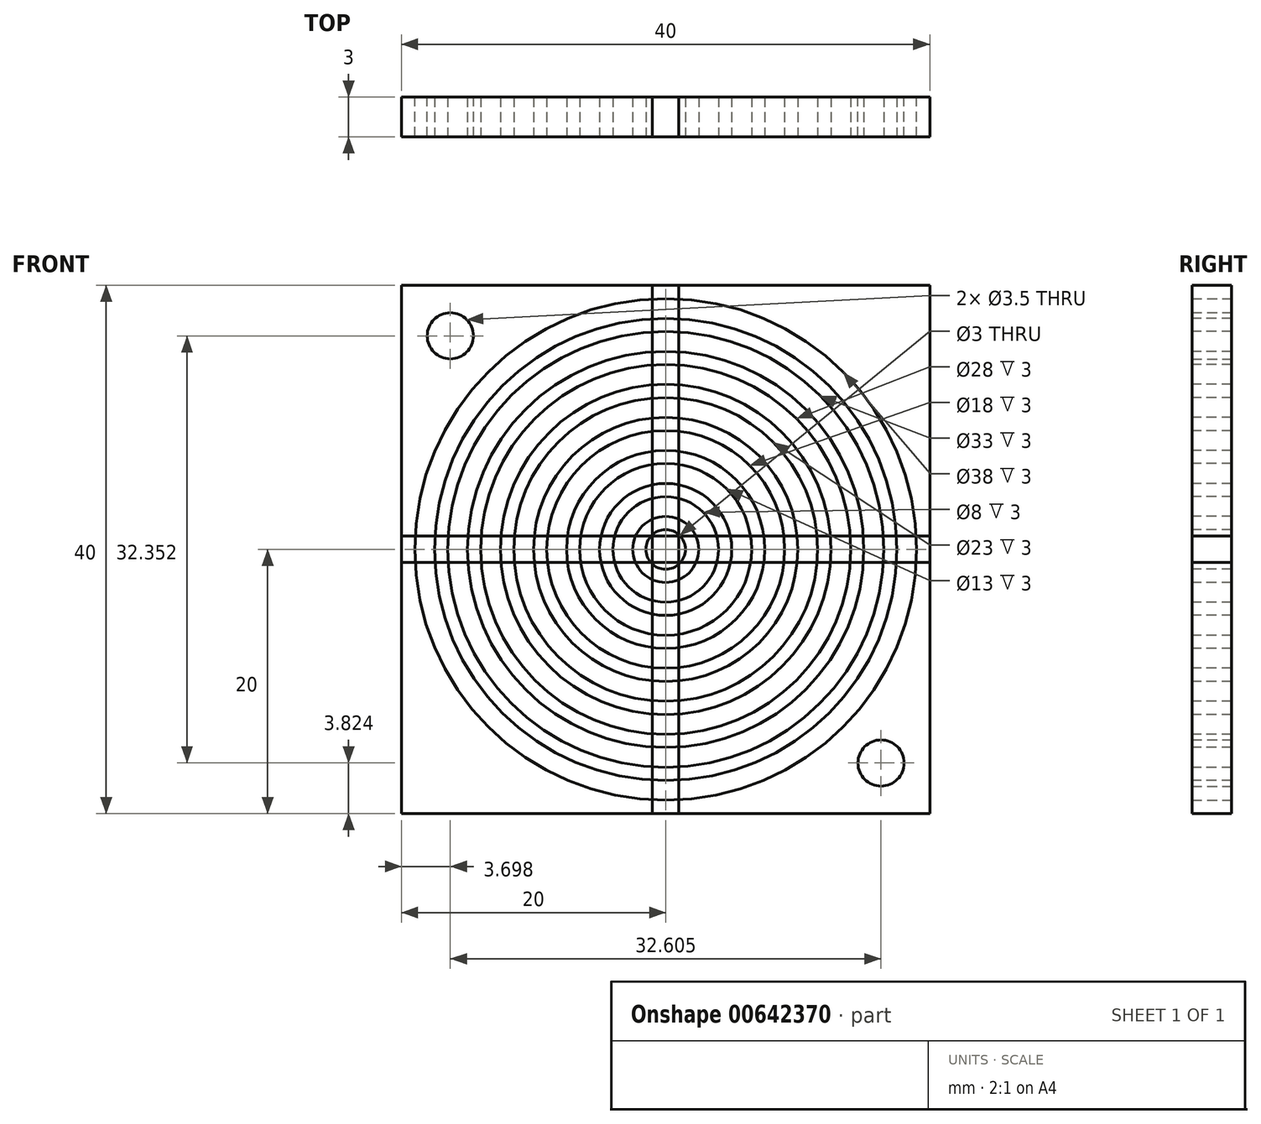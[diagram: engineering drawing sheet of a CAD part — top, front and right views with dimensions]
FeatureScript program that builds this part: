
annotation { "Feature Type Name" : "Feature", "Feature Type Description" : "" }
export const myFeature = defineFeature(function(context is Context, id is Id, definition is map)
    precondition{}
    {
        {
            var Q0;
            Q0=qCreatedBy(makeId("Front.planeOp"),FACE);
            var sketch = newSketch(context, id + "F0", { "sketchPlane" : qUnion([Q0])});
            skLineSegment(sketch, "E0.bottom", {"start": v(-20, 20) * mm, "end": v(20, 20) * mm});
            skLineSegment(sketch, "E0.top", {"start": v(-20, -20) * mm, "end": v(20, -20) * mm});
            skLineSegment(sketch, "E0.left", {"start": v(-20, 20) * mm, "end": v(-20, -20) * mm});
            skLineSegment(sketch, "E0.right", {"start": v(20, 20) * mm, "end": v(20, -20) * mm});
            skPoint(sketch, "E0.middle", {"position": v(0, 0) * mm});
            skCircle(sketch, "E1", {"center": v(0, 0) * mm, "radius": 19 * mm});
            skSolve(sketch);
        }
        {
            var Q0;
            Q0=qSketchRegion(id+"F0",true);
            extrude(context, id + "F1", {"entities" : qUnion([Q0]), "depth" : 3 * mm, "offsetDistance" : 25 * mm});
        }
        {
            var Q0;
            Q0=makeQuery(id+"F1.opExtrude","CAP_FACE",FACE,{"disambiguationData":[OSD([sQuery(id+"F0.wireOp",EDGE,"E0.bottom"),sQuery(id+"F0.wireOp",EDGE,"E0.top"),sQuery(id+"F0.wireOp",EDGE,"E0.left"),sQuery(id+"F0.wireOp",EDGE,"E0.right"),sQuery(id+"F0.wireOp",EDGE,"E1")])],"isStart":true});
            var sketch = newSketch(context, id + "F2", { "sketchPlane" : qUnion([Q0])});
            skCircle(sketch, "E2", {"center": v(16.3, 16.18) * mm, "radius": 1.75 * mm});
            skSolve(sketch);
        }
        {
            var Q0;
            Q0=qSketchRegion(id+"F2",true);
            extrude(context, id + "F3", {"entities" : qUnion([Q0]), "oppositeDirection" : true, "depth" : 5 * mm, "offsetDistance" : 25 * mm});
        }
        {
            var Q0;
            Q0=qCreatedBy(makeId("Top.planeOp"),FACE);
            var sketch = newSketch(context, id + "F5", { "sketchPlane" : qUnion([Q0])});
            skLineSegment(sketch, "E3", {"start": v(0, 9.6) * mm, "end": v(0, -20.04) * mm});
            skSolve(sketch);
        }
        {
            var Q0;
            Q0=makeQuery(id+"F3.opExtrude","SWEPT_BODY",BODY,{"disambiguationData":[OSD([sQuery(id+"F2.wireOp",EDGE,"E2")])]});
            var Q1;
            Q1=makeQuery(id+"F4.opExtrude","SWEPT_BODY",BODY,{"disambiguationData":[OSD([sQuery(id+"Fjy1AtXm3Dg5ggz_1.wireOp",EDGE,"P8TdTz7l-E2nd-Qza4-yqJy-pmsG0hgc4oyG")])]});
            var Q2;
            Q2=sQuery(id+"F5.wireOp",EDGE,"E3");
            circularPattern(context, id + "F6", {"entities" : qUnion([Q0, Q1]), "axis" : qUnion([Q2]), "angle" : 360 * degree, "instanceCount" : 2, "equalSpace" : true});
        }
        {
            var Q0;
            Q0=makeQuery(id+"F6.opPattern","COPY",BODY,{"derivedFrom":makeQuery(id+"F4.opExtrude","SWEPT_BODY",BODY,{"disambiguationData":[OSD([sQuery(id+"Fjy1AtXm3Dg5ggz_1.wireOp",EDGE,"P8TdTz7l-E2nd-Qza4-yqJy-pmsG0hgc4oyG")])]}),"instanceName":"1"});
            var Q1;
            Q1=makeQuery(id+"F6.opPattern","COPY",BODY,{"derivedFrom":makeQuery(id+"F3.opExtrude","SWEPT_BODY",BODY,{"disambiguationData":[OSD([sQuery(id+"F2.wireOp",EDGE,"E2")])]}),"instanceName":"1"});
            var Q2;
            Q2=makeQuery(id+"F4.opExtrude","SWEPT_BODY",BODY,{"disambiguationData":[OSD([sQuery(id+"Fjy1AtXm3Dg5ggz_1.wireOp",EDGE,"P8TdTz7l-E2nd-Qza4-yqJy-pmsG0hgc4oyG")])]});
            var Q3;
            Q3=makeQuery(id+"F3.opExtrude","SWEPT_BODY",BODY,{"disambiguationData":[OSD([sQuery(id+"F2.wireOp",EDGE,"E2")])]});
            var Q4;
            Q4=makeQuery(id+"F1.opExtrude","SWEPT_BODY",BODY,{"disambiguationData":[OSD([sQuery(id+"F0.wireOp",EDGE,"E0.bottom"),sQuery(id+"F0.wireOp",EDGE,"E0.top"),sQuery(id+"F0.wireOp",EDGE,"E0.left"),sQuery(id+"F0.wireOp",EDGE,"E0.right"),sQuery(id+"F0.wireOp",EDGE,"E1")])]});
            booleanBodies(context, id + "F7", {"operationType" : BooleanOperationType.SUBTRACTION, "tools" : qUnion([Q0, Q1, Q2, Q3]), "targets" : qUnion([Q4])});
        }
        {
            var Q0;
            Q0=makeQuery(id+"F1.opExtrude","CAP_FACE",FACE,{"disambiguationData":[OSD([sQuery(id+"F0.wireOp",EDGE,"E0.bottom"),sQuery(id+"F0.wireOp",EDGE,"E0.top"),sQuery(id+"F0.wireOp",EDGE,"E0.left"),sQuery(id+"F0.wireOp",EDGE,"E0.right"),sQuery(id+"F0.wireOp",EDGE,"E1")])],"isStart":false});
            var sketch = newSketch(context, id + "F8", { "sketchPlane" : qUnion([Q0])});
            skCircle(sketch, "E4", {"center": v(0, 0) * mm, "radius": 9 * mm});
            skCircle(sketch, "E5", {"center": v(0, 0) * mm, "radius": 10 * mm});
            skSolve(sketch);
        }
        {
            var Q0;
            Q0=makeQuery(id+"F8.imprint","IMPRINT",FACE,{"disambiguationData":[TD([[makeQuery(id+"F8.imprint","IMPRINT",EDGE,{"derivedFrom":makeQuery(id+"F1.opExtrude","CAP_EDGE",EDGE,{"disambiguationData":[OSD([sQuery(id+"F0.wireOp",EDGE,"E0.bottom")])],"isStart":false})}),-1.0]])]});
            var sketch = newSketch(context, id + "F9", { "sketchPlane" : qUnion([Q0])});
            skCircle(sketch, "E6", {"center": v(0, 0) * mm, "radius": 4 * mm});
            skCircle(sketch, "E7", {"center": v(0, 0) * mm, "radius": 5 * mm});
            skSolve(sketch);
        }
        {
            var Q0;
            Q0=makeQuery(id+"F8.imprint","IMPRINT",FACE,{"disambiguationData":[TD([[makeQuery(id+"F8.imprint","IMPRINT",EDGE,{"derivedFrom":makeQuery(id+"F1.opExtrude","CAP_EDGE",EDGE,{"disambiguationData":[OSD([sQuery(id+"F0.wireOp",EDGE,"E0.bottom")])],"isStart":false})}),-1.0]])]});
            var sketch = newSketch(context, id + "F10", { "sketchPlane" : qUnion([Q0])});
            skCircle(sketch, "E8", {"center": v(0, 0) * mm, "radius": 6.5 * mm});
            skCircle(sketch, "E9", {"center": v(0, 0) * mm, "radius": 7.5 * mm});
            skSolve(sketch);
        }
        {
            var Q0;
            Q0=makeQuery(id+"F8.imprint","IMPRINT",FACE,{"disambiguationData":[TD([[makeQuery(id+"F8.imprint","IMPRINT",EDGE,{"derivedFrom":makeQuery(id+"F1.opExtrude","CAP_EDGE",EDGE,{"disambiguationData":[OSD([sQuery(id+"F0.wireOp",EDGE,"E0.bottom")])],"isStart":false})}),-1.0]])]});
            var sketch = newSketch(context, id + "F11", { "sketchPlane" : qUnion([Q0])});
            skCircle(sketch, "E10", {"center": v(0, 0) * mm, "radius": 1.5 * mm});
            skCircle(sketch, "E11", {"center": v(0, 0) * mm, "radius": 2.5 * mm});
            skSolve(sketch);
        }
        {
            var Q0;
            Q0=makeQuery(id+"F9.imprint","IMPRINT",FACE,{"disambiguationData":[TD([[makeQuery(id+"F9.imprint","IMPRINT",EDGE,{"derivedFrom":makeQuery(id+"F8.imprint","IMPRINT",EDGE,{"derivedFrom":makeQuery(id+"F1.opExtrude","CAP_EDGE",EDGE,{"disambiguationData":[OSD([sQuery(id+"F0.wireOp",EDGE,"E0.bottom")])],"isStart":false})})}),-1.0]])]});
            var sketch = newSketch(context, id + "F12", { "sketchPlane" : qUnion([Q0])});
            skCircle(sketch, "E12", {"center": v(0, 0) * mm, "radius": 2.5 * mm});
            skSolve(sketch);
        }
        {
            var Q0;
            Q0=makeQuery(id+"F8.imprint","IMPRINT",FACE,{"disambiguationData":[TD([[makeQuery(id+"F8.imprint","IMPRINT",EDGE,{"derivedFrom":makeQuery(id+"F1.opExtrude","CAP_EDGE",EDGE,{"disambiguationData":[OSD([sQuery(id+"F0.wireOp",EDGE,"E0.bottom")])],"isStart":false})}),-1.0]])]});
            var sketch = newSketch(context, id + "F13", { "sketchPlane" : qUnion([Q0])});
            skCircle(sketch, "E13", {"center": v(0, 0) * mm, "radius": 11.5 * mm});
            skCircle(sketch, "E14", {"center": v(0, 0) * mm, "radius": 12.5 * mm});
            skSolve(sketch);
        }
        {
            var Q0;
            Q0=makeQuery(id+"F8.imprint","IMPRINT",FACE,{"disambiguationData":[TD([[makeQuery(id+"F8.imprint","IMPRINT",EDGE,{"derivedFrom":makeQuery(id+"F1.opExtrude","CAP_EDGE",EDGE,{"disambiguationData":[OSD([sQuery(id+"F0.wireOp",EDGE,"E0.bottom")])],"isStart":false})}),-1.0]])]});
            var sketch = newSketch(context, id + "F14", { "sketchPlane" : qUnion([Q0])});
            skCircle(sketch, "E15", {"center": v(0, 0) * mm, "radius": 14 * mm});
            skCircle(sketch, "E16", {"center": v(0, 0) * mm, "radius": 15 * mm});
            skSolve(sketch);
        }
        {
            var Q0;
            Q0=makeQuery(id+"F8.imprint","IMPRINT",FACE,{"disambiguationData":[TD([[makeQuery(id+"F8.imprint","IMPRINT",EDGE,{"derivedFrom":makeQuery(id+"F1.opExtrude","CAP_EDGE",EDGE,{"disambiguationData":[OSD([sQuery(id+"F0.wireOp",EDGE,"E0.bottom")])],"isStart":false})}),-1.0]])]});
            var sketch = newSketch(context, id + "F15", { "sketchPlane" : qUnion([Q0])});
            skCircle(sketch, "E17", {"center": v(0, 0) * mm, "radius": 16.5 * mm});
            skCircle(sketch, "E18", {"center": v(0, 0) * mm, "radius": 17.5 * mm});
            skSolve(sketch);
        }
        {
            var Q0;
            Q0=makeQuery(id+"F1.opExtrude","CAP_FACE",FACE,{"disambiguationData":[OSD([sQuery(id+"F0.wireOp",EDGE,"E0.bottom"),sQuery(id+"F0.wireOp",EDGE,"E0.top"),sQuery(id+"F0.wireOp",EDGE,"E0.left"),sQuery(id+"F0.wireOp",EDGE,"E0.right"),sQuery(id+"F0.wireOp",EDGE,"E1")])],"isStart":false});
            var sketch = newSketch(context, id + "F16", { "sketchPlane" : qUnion([Q0])});
            skLineSegment(sketch, "E19.bottom", {"start": v(-1, 20) * mm, "end": v(1, 20) * mm});
            skLineSegment(sketch, "E19.top", {"start": v(-1, -20) * mm, "end": v(1, -20) * mm});
            skLineSegment(sketch, "E19.left", {"start": v(-1, 20) * mm, "end": v(-1, -20) * mm});
            skLineSegment(sketch, "E19.right", {"start": v(1, 20) * mm, "end": v(1, -20) * mm});
            skPoint(sketch, "E19.middle", {"position": v(0, 0) * mm});
            skSolve(sketch);
        }
        {
            var Q0;
            {var subQ0=makeQuery(id+"F1.opExtrude","CAP_EDGE",EDGE,{"disambiguationData":[OSD([sQuery(id+"F0.wireOp",EDGE,"E0.right")])],"isStart":false});Q0=makeQuery(id+"F16.imprint","IMPRINT",FACE,{"disambiguationData":[TD([[makeQuery(id+"F16.imprint","IMPRINT",EDGE,{"derivedFrom":subQ0}),-1.0]])]});}
            var sketch = newSketch(context, id + "F17", { "sketchPlane" : qUnion([Q0])});
            skLineSegment(sketch, "E20.bottom", {"start": v(-20, 1) * mm, "end": v(20, 1) * mm});
            skLineSegment(sketch, "E20.top", {"start": v(-20, -1) * mm, "end": v(20, -1) * mm});
            skLineSegment(sketch, "E20.left", {"start": v(-20, 1) * mm, "end": v(-20, -1) * mm});
            skLineSegment(sketch, "E20.right", {"start": v(20, 1) * mm, "end": v(20, -1) * mm});
            skPoint(sketch, "E20.middle", {"position": v(0, 0) * mm});
            skSolve(sketch);
        }
        {
            var Q0;
            Q0=qSketchRegion(id+"F8",true);
            var Q1;
            Q1=qSketchRegion(id+"F9",true);
            var Q2;
            Q2=qSketchRegion(id+"F10",true);
            var Q3;
            Q3=qSketchRegion(id+"F11",true);
            var Q4;
            Q4=qSketchRegion(id+"F12",true);
            var Q5;
            Q5=qSketchRegion(id+"F13",true);
            var Q6;
            Q6=qSketchRegion(id+"F14",true);
            var Q7;
            Q7=qSketchRegion(id+"F15",true);
            var Q8;
            Q8=qSketchRegion(id+"F16",true);
            var Q9;
            Q9=qSketchRegion(id+"F17",true);
            extrude(context, id + "F18", {"entities" : qUnion([Q0, Q1, Q2, Q3, Q4, Q5, Q6, Q7, Q8, Q9]), "oppositeDirection" : true, "depth" : 3 * mm, "offsetDistance" : 25 * mm});
        }
    });
